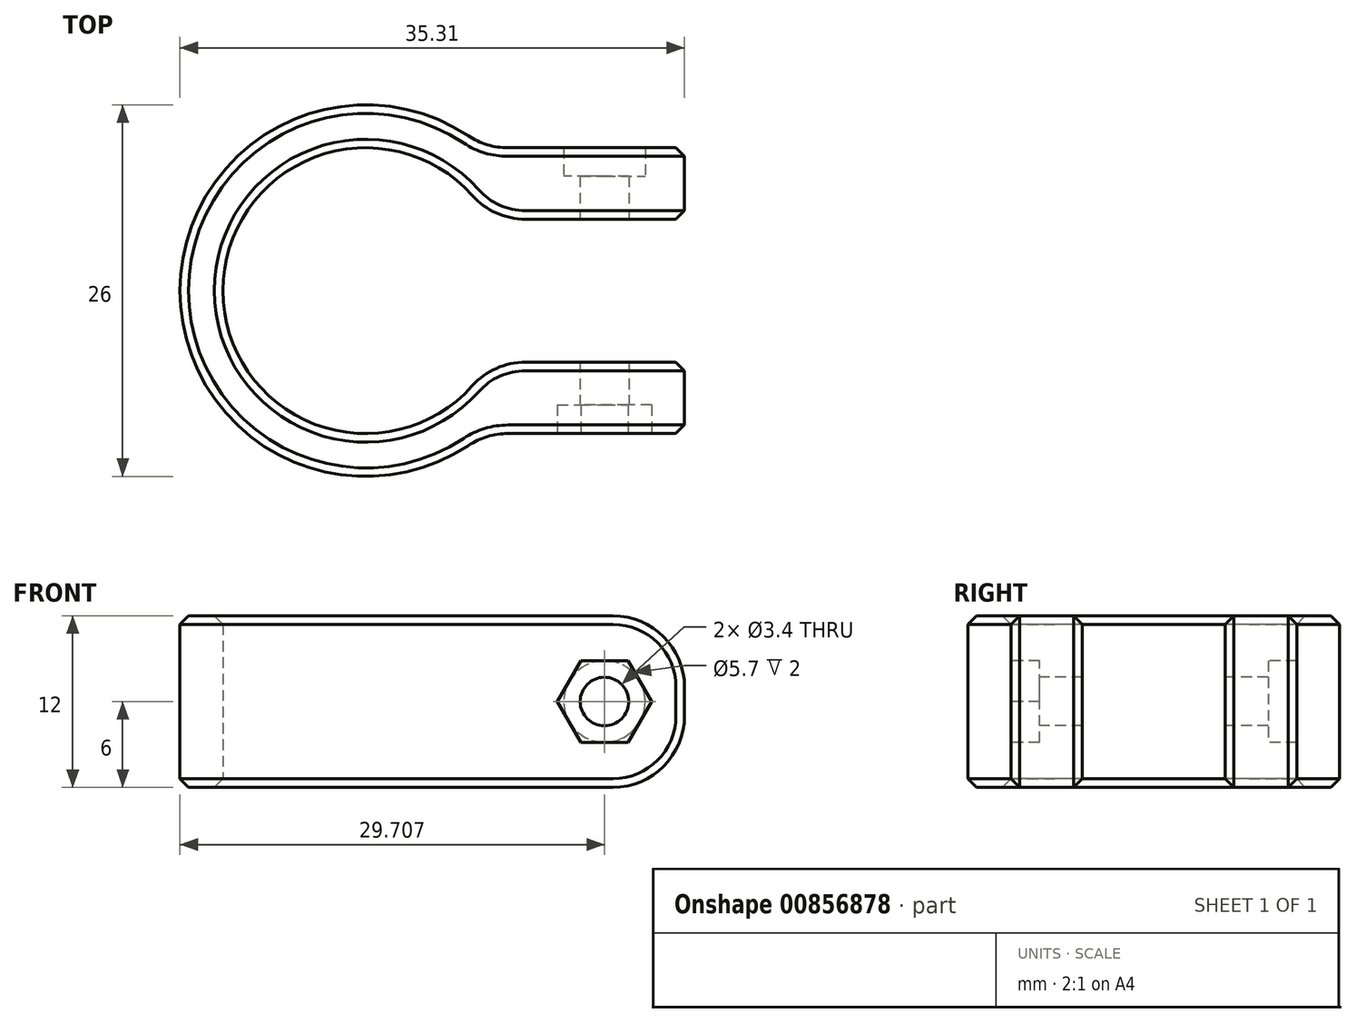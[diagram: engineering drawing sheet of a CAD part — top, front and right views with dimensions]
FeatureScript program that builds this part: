
annotation { "Feature Type Name" : "Feature", "Feature Type Description" : "" }
export const myFeature = defineFeature(function(context is Context, id is Id, definition is map)
    precondition{}
    {
        {
            var Q0;
            Q0=qCreatedBy(makeId("Top.planeOp"),FACE);
            var sketch = newSketch(context, id + "F0", { "sketchPlane" : qUnion([Q0])});
            skCircle(sketch, "E0", {"center": v(0, 0) * mm, "radius": 10 * mm});
            skCircle(sketch, "E1", {"center": v(0, 0) * mm, "radius": 13 * mm});
            skLineSegment(sketch, "E2", {"start": v(8.66, 5) * mm, "end": v(12, 5) * mm});
            skLineSegment(sketch, "E3.MirrorCS", {"start": v(8.66, -5) * mm, "end": v(12, -5) * mm});
            skLineSegment(sketch, "E4.bottom", {"start": v(22.3, 5) * mm, "end": v(8.3, 5) * mm});
            skLineSegment(sketch, "E4.top", {"start": v(22.3, 10) * mm, "end": v(8.3, 10) * mm});
            skLineSegment(sketch, "E4.left", {"start": v(22.3, 5) * mm, "end": v(22.3, 10) * mm});
            skLineSegment(sketch, "E4.right", {"start": v(8.3, 5) * mm, "end": v(8.3, 10) * mm});
            skLineSegment(sketch, "E5.MirrorCS", {"start": v(22.3, -5) * mm, "end": v(8.3, -5) * mm});
            skLineSegment(sketch, "E6.MirrorCS", {"start": v(22.3, -5) * mm, "end": v(22.3, -10) * mm});
            skLineSegment(sketch, "E7.MirrorCS", {"start": v(22.3, -10) * mm, "end": v(8.3, -10) * mm});
            skLineSegment(sketch, "E8.MirrorCS", {"start": v(8.3, -5) * mm, "end": v(8.3, -10) * mm});
            skSolve(sketch);
        }
        {
            var Q0;
            {var subQ1=sQuery(id+"F0.wireOp",EDGE,"E2");Q0=makeQuery(id+"F0.imprint","IMPRINT",FACE,{"disambiguationData":[TD([[makeQuery(id+"F0.imprint","IMPRINT",EDGE,{"derivedFrom":subQ1}),1.0]])]});}
            var Q1;
            {var subQ0=sQuery(id+"F0.wireOp",EDGE,"E4.top");Q1=makeQuery(id+"F0.imprint","IMPRINT",FACE,{"disambiguationData":[TD([[makeQuery(id+"F0.imprint","IMPRINT",EDGE,{"derivedFrom":subQ0}),1.0]])]});}
            var Q2;
            {var subQ4=sQuery(id+"F0.wireOp",EDGE,"E6.MirrorCS");Q2=makeQuery(id+"F0.imprint","IMPRINT",FACE,{"disambiguationData":[TD([[makeQuery(id+"F0.imprint","IMPRINT",EDGE,{"derivedFrom":subQ4}),-1.0]])]});}
            var Q3;
            {var subQ0=sQuery(id+"F0.wireOp",EDGE,"E4.right");var subQ1=sQuery(id+"F0.wireOp",EDGE,"E0");var subQ2=makeQuery(id+"F0.imprint","INTERSECT",VERTEX,{"derivedFrom":[subQ1,subQ0]});Q3=makeQuery(id+"F0.imprint","IMPRINT",FACE,{"disambiguationData":[TD([[makeQuery(id+"F0.imprint","IMPRINT",EDGE,{"disambiguationData":[TD([[subQ2,-1.0]])],"derivedFrom":subQ1}),-1.0]])]});}
            var Q4;
            {var subQ0=sQuery(id+"F0.wireOp",EDGE,"E4.right");var subQ1=sQuery(id+"F0.wireOp",EDGE,"E0");var subQ2=makeQuery(id+"F0.imprint","INTERSECT",VERTEX,{"derivedFrom":[subQ1,subQ0]});Q4=makeQuery(id+"F0.imprint","IMPRINT",FACE,{"disambiguationData":[TD([[makeQuery(id+"F0.imprint","IMPRINT",EDGE,{"disambiguationData":[TD([[subQ2,1.0]])],"derivedFrom":subQ1}),-1.0]])]});}
            var Q5;
            {var subQ0=sQuery(id+"F0.wireOp",EDGE,"E8.MirrorCS");var subQ1=sQuery(id+"F0.wireOp",EDGE,"E0");var subQ2=makeQuery(id+"F0.imprint","INTERSECT",VERTEX,{"derivedFrom":[subQ1,subQ0]});Q5=makeQuery(id+"F0.imprint","IMPRINT",FACE,{"disambiguationData":[TD([[makeQuery(id+"F0.imprint","IMPRINT",EDGE,{"disambiguationData":[TD([[subQ2,-1.0]])],"derivedFrom":subQ1}),-1.0]])]});}
            extrude(context, id + "F1", {"entities" : qUnion([Q0, Q1, Q2, Q3, Q4, Q5]), "depth" : 12 * mm, "offsetDistance" : 25 * mm});
        }
        {
            var Q0;
            Q0=makeQuery(id+"F1.opExtrude","SWEPT_EDGE",EDGE,{"disambiguationData":[OSD([sQuery(id+"F0.wireOp",EDGE,"E1"),sQuery(id+"F0.wireOp",EDGE,"E7.MirrorCS"),sQuery(id+"F0.wireOp",EDGE,"E8.MirrorCS")])]});
            var Q1;
            Q1=makeQuery(id+"F1.opExtrude","SWEPT_EDGE",EDGE,{"disambiguationData":[OSD([sQuery(id+"F0.wireOp",EDGE,"E1"),sQuery(id+"F0.wireOp",EDGE,"E4.top"),sQuery(id+"F0.wireOp",EDGE,"E4.right")])]});
            var Q2;
            Q2=makeQuery(id+"F1.opExtrude","SWEPT_EDGE",EDGE,{"disambiguationData":[OSD([sQuery(id+"F0.wireOp",EDGE,"E0"),sQuery(id+"F0.wireOp",EDGE,"E3.MirrorCS")])]});
            var Q3;
            Q3=makeQuery(id+"F1.opExtrude","SWEPT_EDGE",EDGE,{"disambiguationData":[OSD([sQuery(id+"F0.wireOp",EDGE,"E0"),sQuery(id+"F0.wireOp",EDGE,"E2")])]});
            fillet(context, id + "F2", {"entities" : qUnion([Q0, Q1, Q2, Q3]), "radius" : 5 * mm, "tangentPropagation" : true, "allowEdgeOverflow" : false});
        }
        {
            var Q0;
            Q0=makeQuery(id+"F1.opExtrude","CAP_EDGE",EDGE,{"disambiguationData":[OSD([sQuery(id+"F0.wireOp",EDGE,"E6.MirrorCS")])],"isStart":false});
            var Q1;
            Q1=makeQuery(id+"F1.opExtrude","CAP_EDGE",EDGE,{"disambiguationData":[OSD([sQuery(id+"F0.wireOp",EDGE,"E4.left")])],"isStart":false});
            var Q2;
            Q2=makeQuery(id+"F1.opExtrude","CAP_EDGE",EDGE,{"disambiguationData":[OSD([sQuery(id+"F0.wireOp",EDGE,"E6.MirrorCS")])],"isStart":true});
            var Q3;
            Q3=makeQuery(id+"F1.opExtrude","CAP_EDGE",EDGE,{"disambiguationData":[OSD([sQuery(id+"F0.wireOp",EDGE,"E4.left")])],"isStart":true});
            fillet(context, id + "F3", {"entities" : qUnion([Q0, Q1, Q2, Q3]), "radius" : 5 * mm, "tangentPropagation" : true, "allowEdgeOverflow" : false});
        }
        {
            var Q0;
            Q0=makeQuery(id+"F1.opExtrude","CAP_EDGE",EDGE,{"disambiguationData":[OSD([sQuery(id+"F0.wireOp",EDGE,"E0")])],"isStart":false});
            var Q1;
            Q1=makeQuery(id+"F1.opExtrude","CAP_EDGE",EDGE,{"disambiguationData":[OSD([sQuery(id+"F0.wireOp",EDGE,"E1")])],"isStart":false});
            var Q2;
            Q2=makeQuery(id+"F1.opExtrude","CAP_EDGE",EDGE,{"disambiguationData":[OSD([sQuery(id+"F0.wireOp",EDGE,"E1")])],"isStart":true});
            var Q3;
            Q3=makeQuery(id+"F1.opExtrude","CAP_EDGE",EDGE,{"disambiguationData":[OSD([sQuery(id+"F0.wireOp",EDGE,"E0")])],"isStart":true});
            chamfer(context, id + "F4", {"entities" : qUnion([Q0, Q1, Q2, Q3]), "width" : .6 * mm, "tangentPropagation" : true});
        }
        {
            var Q0;
            Q0=makeQuery(id+"F1.opExtrude","SWEPT_FACE",FACE,{"disambiguationData":[OSD([sQuery(id+"F0.wireOp",EDGE,"E7.MirrorCS")])]});
            var sketch = newSketch(context, id + "F5", { "sketchPlane" : qUnion([Q0])});
            skCircle(sketch, "E9", {"center": v(16.7, 6) * mm, "radius": 1.7 * mm});
            skPoint(sketch, "E9.centerSnap0", {"position": v(21.7, 6) * mm});
            skCircle(sketch, "E10.cCircle", {"center": v(16.7, 6) * mm, "radius": 2.85 * mm});
            skLineSegment(sketch, "E10.0", {"start": v(18.35, 3.15) * mm, "end": v(15.06, 3.15) * mm});
            skLineSegment(sketch, "E10.1", {"start": v(15.06, 3.15) * mm, "end": v(13.42, 6) * mm});
            skLineSegment(sketch, "E10.2", {"start": v(13.42, 6) * mm, "end": v(15.06, 8.85) * mm});
            skLineSegment(sketch, "E10.3", {"start": v(15.06, 8.85) * mm, "end": v(18.35, 8.85) * mm});
            skLineSegment(sketch, "E10.4", {"start": v(18.35, 8.85) * mm, "end": v(20, 6) * mm});
            skLineSegment(sketch, "E10.5", {"start": v(20, 6) * mm, "end": v(18.35, 3.15) * mm});
            skPoint(sketch, "E10.0.midPoint", {"position": v(16.7, 3.15) * mm});
            skSolve(sketch);
        }
        {
            var Q0;
            Q0=makeQuery(id+"F5.imprint","IMPRINT",FACE,{"disambiguationData":[TD([[makeQuery(id+"F5.imprint","IMPRINT",EDGE,{"derivedFrom":sQuery(id+"F5.wireOp",EDGE,"E9")}),1.0]])]});
            extrude(context, id + "F6", {"entities" : qUnion([Q0]), "operationType" : NewBodyOperationType.REMOVE, "endBound" : BoundingType.THROUGH_ALL, "oppositeDirection" : true, "depth" : 25 * mm, "offsetDistance" : 25 * mm});
        }
        {
            var Q0;
            Q0=makeQuery(id+"F5.imprint","IMPRINT",FACE,{"disambiguationData":[TD([[makeQuery(id+"F5.imprint","IMPRINT",EDGE,{"derivedFrom":sQuery(id+"F5.wireOp",EDGE,"E9")}),-1.0]])]});
            var Q1;
            {var subQ0=sQuery(id+"F5.wireOp",EDGE,"E10.1");var subQ1=sQuery(id+"F5.wireOp",EDGE,"E10.cCircle");var subQ2=makeQuery(id+"F5.imprint","INTERSECT",VERTEX,{"derivedFrom":[subQ1,subQ0]});Q1=makeQuery(id+"F5.imprint","IMPRINT",FACE,{"disambiguationData":[TD([[makeQuery(id+"F5.imprint","IMPRINT",EDGE,{"disambiguationData":[TD([[subQ2,-1.0]])],"derivedFrom":subQ1}),-1.0]])]});}
            var Q2;
            {var subQ0=sQuery(id+"F5.wireOp",EDGE,"E10.0");var subQ1=sQuery(id+"F5.wireOp",EDGE,"E10.cCircle");var subQ2=makeQuery(id+"F5.imprint","INTERSECT",VERTEX,{"derivedFrom":[subQ1,subQ0]});Q2=makeQuery(id+"F5.imprint","IMPRINT",FACE,{"disambiguationData":[TD([[makeQuery(id+"F5.imprint","IMPRINT",EDGE,{"disambiguationData":[TD([[subQ2,-1.0]])],"derivedFrom":subQ1}),-1.0]])]});}
            var Q3;
            {var subQ0=sQuery(id+"F5.wireOp",EDGE,"E10.4");var subQ1=sQuery(id+"F5.wireOp",EDGE,"E10.cCircle");var subQ2=makeQuery(id+"F5.imprint","INTERSECT",VERTEX,{"derivedFrom":[subQ1,subQ0]});Q3=makeQuery(id+"F5.imprint","IMPRINT",FACE,{"disambiguationData":[TD([[makeQuery(id+"F5.imprint","IMPRINT",EDGE,{"disambiguationData":[TD([[subQ2,1.0]])],"derivedFrom":subQ1}),-1.0]])]});}
            var Q4;
            {var subQ0=sQuery(id+"F5.wireOp",EDGE,"E10.3");var subQ1=sQuery(id+"F5.wireOp",EDGE,"E10.cCircle");var subQ2=makeQuery(id+"F5.imprint","INTERSECT",VERTEX,{"derivedFrom":[subQ1,subQ0]});Q4=makeQuery(id+"F5.imprint","IMPRINT",FACE,{"disambiguationData":[TD([[makeQuery(id+"F5.imprint","IMPRINT",EDGE,{"disambiguationData":[TD([[subQ2,1.0]])],"derivedFrom":subQ1}),-1.0]])]});}
            var Q5;
            {var subQ0=sQuery(id+"F5.wireOp",EDGE,"E10.2");var subQ1=sQuery(id+"F5.wireOp",EDGE,"E10.cCircle");var subQ2=makeQuery(id+"F5.imprint","INTERSECT",VERTEX,{"derivedFrom":[subQ1,subQ0]});Q5=makeQuery(id+"F5.imprint","IMPRINT",FACE,{"disambiguationData":[TD([[makeQuery(id+"F5.imprint","IMPRINT",EDGE,{"disambiguationData":[TD([[subQ2,-1.0]])],"derivedFrom":subQ1}),-1.0]])]});}
            var Q6;
            {var subQ0=sQuery(id+"F5.wireOp",EDGE,"E10.3");var subQ1=sQuery(id+"F5.wireOp",EDGE,"E10.cCircle");var subQ2=makeQuery(id+"F5.imprint","INTERSECT",VERTEX,{"derivedFrom":[subQ1,subQ0]});Q6=makeQuery(id+"F5.imprint","IMPRINT",FACE,{"disambiguationData":[TD([[makeQuery(id+"F5.imprint","IMPRINT",EDGE,{"disambiguationData":[TD([[subQ2,-1.0]])],"derivedFrom":subQ1}),-1.0]])]});}
            extrude(context, id + "F7", {"entities" : qUnion([Q0, Q1, Q2, Q3, Q4, Q5, Q6]), "operationType" : NewBodyOperationType.REMOVE, "oppositeDirection" : true, "depth" : 2 * mm, "offsetDistance" : 25 * mm});
        }
        {
            var Q0;
            Q0=makeQuery(id+"F5.imprint","IMPRINT",FACE,{"disambiguationData":[TD([[makeQuery(id+"F5.imprint","IMPRINT",EDGE,{"derivedFrom":sQuery(id+"F5.wireOp",EDGE,"E9")}),-1.0]])]});
            var Q1;
            Q1=makeQuery(id+"F1.opExtrude","SWEPT_FACE",FACE,{"disambiguationData":[OSD([sQuery(id+"F0.wireOp",EDGE,"E4.top")])]});
            var Q2;
            Q2=makeQuery(id+"F1.opExtrude","SWEPT_FACE",FACE,{"disambiguationData":[OSD([sQuery(id+"F0.wireOp",EDGE,"E2"),sQuery(id+"F0.wireOp",EDGE,"E4.bottom")])]});
            extrude(context, id + "F8", {"entities" : qUnion([Q0]), "operationType" : NewBodyOperationType.REMOVE, "endBound" : BoundingType.UP_TO_SURFACE, "oppositeDirection" : true, "depth" : 20.2 * mm, "endBoundEntityFace" : qUnion([Q1]), "offsetDistance" : 25 * mm, "hasSecondDirection" : true, "secondDirectionBound" : SecondDirectionBoundingType.UP_TO_SURFACE, "secondDirectionOppositeDirection" : true, "secondDirectionDepth" : 15.7 * mm, "secondDirectionBoundEntityFace" : qUnion([Q2]), "hasSecondDirectionOffset" : true, "secondDirectionOffsetDistance" : -3 * mm});
        }
    });
